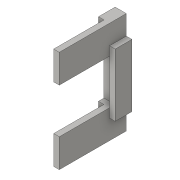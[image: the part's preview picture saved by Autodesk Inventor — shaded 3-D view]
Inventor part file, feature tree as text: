
AUTODESK INVENTOR PART (.ipt)
format: ipt  version: 2016 (Build 200138000, 138)  size: 108,544 bytes
history: native  units: mm
features: extrude x3, sketch x3
ambient origin geometry x8: Origin, YZ Plane, XZ Plane, XY Plane, X Axis, Y Axis, Z Axis, Center Point
bodies: Solid1 (feature_tree)
feature tree (6):
  extrude  "Extrusion1"  Depth=20.0mm
  extrude  "Extrusion2"  Depth=20.0mm
  extrude  "Extrusion3"  Depth=20.0mm
  sketch  "Sketch1"  dims[d16=35.0mm d17=20.0mm]
  sketch  "Sketch2"  dims[d18=35.0mm d19=20.0mm]
  sketch  "Sketch3"  dims[d20=30.0mm d21=0.0mm d22=20.0mm d23=80.0mm d25=16.0mm d26=10.0mm d27=0.0mm d28=112.0mm d29=10.0mm d30=51.0mm d31=10.0mm d32=51.0mm d33=90.0mm d34=0.0mm d35=10.0mm]
